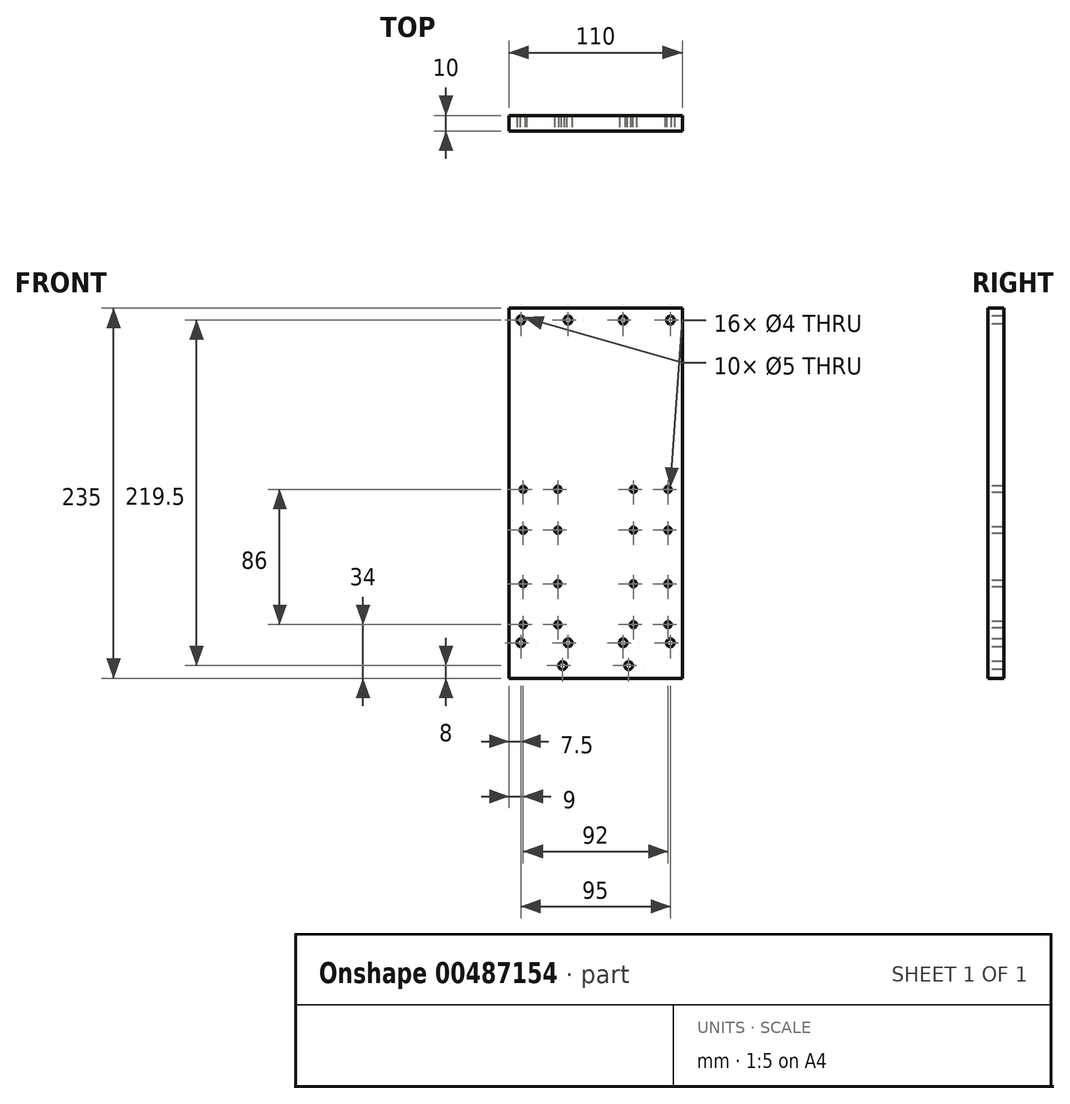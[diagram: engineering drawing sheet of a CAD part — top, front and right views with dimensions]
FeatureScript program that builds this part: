
annotation { "Feature Type Name" : "Feature", "Feature Type Description" : "" }
export const myFeature = defineFeature(function(context is Context, id is Id, definition is map)
    precondition{}
    {
        {
            var Q0;
            Q0=qCreatedBy(makeId("Front.planeOp"),FACE);
            var sketch = newSketch(context, id + "F0", { "sketchPlane" : qUnion([Q0])});
            skLineSegment(sketch, "E0.bottom", {"start": v(-55, 47) * mm, "end": v(55, 47) * mm});
            skLineSegment(sketch, "E0.top", {"start": v(-55, -47) * mm, "end": v(55, -47) * mm});
            skLineSegment(sketch, "E0.left", {"start": v(-55, 47) * mm, "end": v(-55, -47) * mm});
            skLineSegment(sketch, "E0.right", {"start": v(55, 47) * mm, "end": v(55, -47) * mm});
            skSolve(sketch);
        }
        {
            var Q0;
            Q0 = qSketchRegion(id + "F0", true);
            extrude(context, id + "F1", {"entities" : qUnion([Q0]), "depth" : 10 * mm});
        }
        {
            var Q0;
            Q0=makeQuery(id+"F1.opExtrude","CAP_FACE",FACE,{"disambiguationData":[OSD([sQuery(id+"F0.wireOp",EDGE,"E0.bottom"),sQuery(id+"F0.wireOp",EDGE,"E0.top"),sQuery(id+"F0.wireOp",EDGE,"E0.left"),sQuery(id+"F0.wireOp",EDGE,"E0.right")])],"isStart":false});
            var sketch = newSketch(context, id + "F2", { "sketchPlane" : qUnion([Q0])});
            skCircle(sketch, "E1", {"center": v(-46, 43) * mm, "radius": 2 * mm});
            skCircle(sketch, "E2", {"center": v(-24, 43) * mm, "radius": 2 * mm});
            skCircle(sketch, "E3", {"center": v(-46, 17) * mm, "radius": 2 * mm});
            skCircle(sketch, "E4", {"center": v(-24, 17) * mm, "radius": 2 * mm});
            skCircle(sketch, "E5.MirrorC", {"center": v(46, 43) * mm, "radius": 2 * mm});
            skCircle(sketch, "E6.MirrorC", {"center": v(24, 43) * mm, "radius": 2 * mm});
            skCircle(sketch, "E7.MirrorC", {"center": v(24, 17) * mm, "radius": 2 * mm});
            skCircle(sketch, "E8.MirrorC", {"center": v(46, 17) * mm, "radius": 2 * mm});
            skCircle(sketch, "E9.MirrorC", {"center": v(-46, -17) * mm, "radius": 2 * mm});
            skCircle(sketch, "E10.MirrorC", {"center": v(-46, -43) * mm, "radius": 2 * mm});
            skCircle(sketch, "E11.MirrorC", {"center": v(-24, -43) * mm, "radius": 2 * mm});
            skCircle(sketch, "E12.MirrorC", {"center": v(-24, -17) * mm, "radius": 2 * mm});
            skCircle(sketch, "E13.MirrorC", {"center": v(24, -17) * mm, "radius": 2 * mm});
            skCircle(sketch, "E14.MirrorC", {"center": v(24, -43) * mm, "radius": 2 * mm});
            skCircle(sketch, "E15.MirrorC", {"center": v(46, -43) * mm, "radius": 2 * mm});
            skCircle(sketch, "E16.MirrorC", {"center": v(46, -17) * mm, "radius": 2 * mm});
            skSolve(sketch);
        }
        {
            var Q0;
            Q0 = qSketchRegion(id + "F2", true);
            extrude(context, id + "F3", {"entities" : qUnion([Q0]), "operationType" : NewBodyOperationType.REMOVE, "oppositeDirection" : true, "depth" : 25 * mm});
        }
        {
            var Q0;
            Q0=qCreatedBy(makeId("Front.planeOp"),FACE);
            var sketch = newSketch(context, id + "F4", { "sketchPlane" : qUnion([Q0])});
            skLineSegment(sketch, "E17.bottom", {"start": v(-55, 47) * mm, "end": v(55, 47) * mm});
            skLineSegment(sketch, "E17.top", {"start": v(-55, 158) * mm, "end": v(55, 158) * mm});
            skLineSegment(sketch, "E17.left", {"start": v(-55, 47) * mm, "end": v(-55, 158) * mm});
            skLineSegment(sketch, "E17.right", {"start": v(55, 47) * mm, "end": v(55, 158) * mm});
            skLineSegment(sketch, "E18.bottom", {"start": v(-55, -47) * mm, "end": v(55, -47) * mm});
            skLineSegment(sketch, "E18.top", {"start": v(-55, -62) * mm, "end": v(55, -62) * mm});
            skLineSegment(sketch, "E18.left", {"start": v(-55, -47) * mm, "end": v(-55, -62) * mm});
            skLineSegment(sketch, "E18.right", {"start": v(55, -47) * mm, "end": v(55, -62) * mm});
            skSolve(sketch);
        }
        {
            var Q0;
            Q0 = qSketchRegion(id + "F4", true);
            extrude(context, id + "F5", {"entities" : qUnion([Q0]), "operationType" : NewBodyOperationType.ADD, "depth" : 10 * mm});
        }
        {
            var Q0;
            Q0=makeQuery(id+"F5.boolean.opBoolean","MERGE",FACE,{"derivedFrom":[makeQuery(id+"F1.opExtrude","CAP_FACE",FACE,{"disambiguationData":[OSD([sQuery(id+"F0.wireOp",EDGE,"E0.bottom"),sQuery(id+"F0.wireOp",EDGE,"E0.top"),sQuery(id+"F0.wireOp",EDGE,"E0.left"),sQuery(id+"F0.wireOp",EDGE,"E0.right")])],"isStart":false}),makeQuery(id+"F5.opExtrude","CAP_FACE",FACE,{"disambiguationData":[OSD([sQuery(id+"F4.wireOp",EDGE,"E17.bottom"),sQuery(id+"F4.wireOp",EDGE,"E17.top"),sQuery(id+"F4.wireOp",EDGE,"E17.left"),sQuery(id+"F4.wireOp",EDGE,"E17.right")])],"isStart":false}),makeQuery(id+"F5.opExtrude","CAP_FACE",FACE,{"disambiguationData":[OSD([sQuery(id+"F4.wireOp",EDGE,"E18.bottom"),sQuery(id+"F4.wireOp",EDGE,"E18.top"),sQuery(id+"F4.wireOp",EDGE,"E18.left"),sQuery(id+"F4.wireOp",EDGE,"E18.right")])],"isStart":false})]});
            var sketch = newSketch(context, id + "F6", { "sketchPlane" : qUnion([Q0])});
            skCircle(sketch, "E19", {"center": v(-47.5, -54.5) * mm, "radius": 2.5 * mm});
            skCircle(sketch, "E20", {"center": v(-17.5, -54.5) * mm, "radius": 2.5 * mm});
            skCircle(sketch, "E21", {"center": v(17.5, -54.5) * mm, "radius": 2.5 * mm});
            skCircle(sketch, "E22", {"center": v(47.5, -54.5) * mm, "radius": 2.5 * mm});
            skCircle(sketch, "E23", {"center": v(-47.5, 150.5) * mm, "radius": 2.5 * mm});
            skCircle(sketch, "E24", {"center": v(-17.5, 150.5) * mm, "radius": 2.5 * mm});
            skCircle(sketch, "E25", {"center": v(17.5, 150.5) * mm, "radius": 2.5 * mm});
            skCircle(sketch, "E26", {"center": v(47.5, 150.5) * mm, "radius": 2.5 * mm});
            skSolve(sketch);
        }
        {
            var Q0;
            Q0 = qSketchRegion(id + "F6", true);
            extrude(context, id + "F7", {"entities" : qUnion([Q0]), "operationType" : NewBodyOperationType.REMOVE, "oppositeDirection" : true, "depth" : 25 * mm});
        }
        {
            var Q0;
            Q0=qCreatedBy(makeId("Front.planeOp"),FACE);
            var sketch = newSketch(context, id + "F8", { "sketchPlane" : qUnion([Q0])});
            skLineSegment(sketch, "E27.bottom", {"start": v(-55, -62) * mm, "end": v(55, -62) * mm});
            skLineSegment(sketch, "E27.top", {"start": v(-55, -77) * mm, "end": v(55, -77) * mm});
            skLineSegment(sketch, "E27.left", {"start": v(-55, -62) * mm, "end": v(-55, -77) * mm});
            skLineSegment(sketch, "E27.right", {"start": v(55, -62) * mm, "end": v(55, -77) * mm});
            skSolve(sketch);
        }
        {
            var Q0;
            Q0 = qSketchRegion(id + "F8", true);
            extrude(context, id + "F9", {"entities" : qUnion([Q0]), "operationType" : NewBodyOperationType.ADD, "depth" : 10 * mm});
        }
        {
            var Q0;
            Q0=makeQuery(id+"F5.boolean.opBoolean","MERGE",FACE,{"derivedFrom":[makeQuery(id+"F1.opExtrude","CAP_FACE",FACE,{"disambiguationData":[OSD([sQuery(id+"F0.wireOp",EDGE,"E0.bottom"),sQuery(id+"F0.wireOp",EDGE,"E0.top"),sQuery(id+"F0.wireOp",EDGE,"E0.left"),sQuery(id+"F0.wireOp",EDGE,"E0.right")])],"isStart":false}),makeQuery(id+"F5.opExtrude","CAP_FACE",FACE,{"disambiguationData":[OSD([sQuery(id+"F4.wireOp",EDGE,"E17.bottom"),sQuery(id+"F4.wireOp",EDGE,"E17.top"),sQuery(id+"F4.wireOp",EDGE,"E17.left"),sQuery(id+"F4.wireOp",EDGE,"E17.right")])],"isStart":false}),makeQuery(id+"F5.opExtrude","CAP_FACE",FACE,{"disambiguationData":[OSD([sQuery(id+"F4.wireOp",EDGE,"E18.bottom"),sQuery(id+"F4.wireOp",EDGE,"E18.top"),sQuery(id+"F4.wireOp",EDGE,"E18.left"),sQuery(id+"F4.wireOp",EDGE,"E18.right")])],"isStart":false})]});
            var sketch = newSketch(context, id + "F10", { "sketchPlane" : qUnion([Q0])});
            skCircle(sketch, "E28", {"center": v(-21, -69) * mm, "radius": 2.5 * mm});
            skCircle(sketch, "E29", {"center": v(21, -69) * mm, "radius": 2.5 * mm});
            skSolve(sketch);
        }
        {
            var Q0;
            Q0=makeQuery(id+"F10.imprint","IMPRINT",FACE,{"disambiguationData":[TD([[makeQuery(id+"F10.imprint","IMPRINT",EDGE,{"derivedFrom":sQuery(id+"F10.wireOp",EDGE,"E28")}),1.0]])]});
            var Q1;
            Q1=makeQuery(id+"F10.imprint","IMPRINT",FACE,{"disambiguationData":[TD([[makeQuery(id+"F10.imprint","IMPRINT",EDGE,{"derivedFrom":sQuery(id+"F10.wireOp",EDGE,"E29")}),1.0]])]});
            extrude(context, id + "F11", {"entities" : qUnion([Q0, Q1]), "operationType" : NewBodyOperationType.REMOVE, "oppositeDirection" : true, "depth" : 25 * mm});
        }
    });
